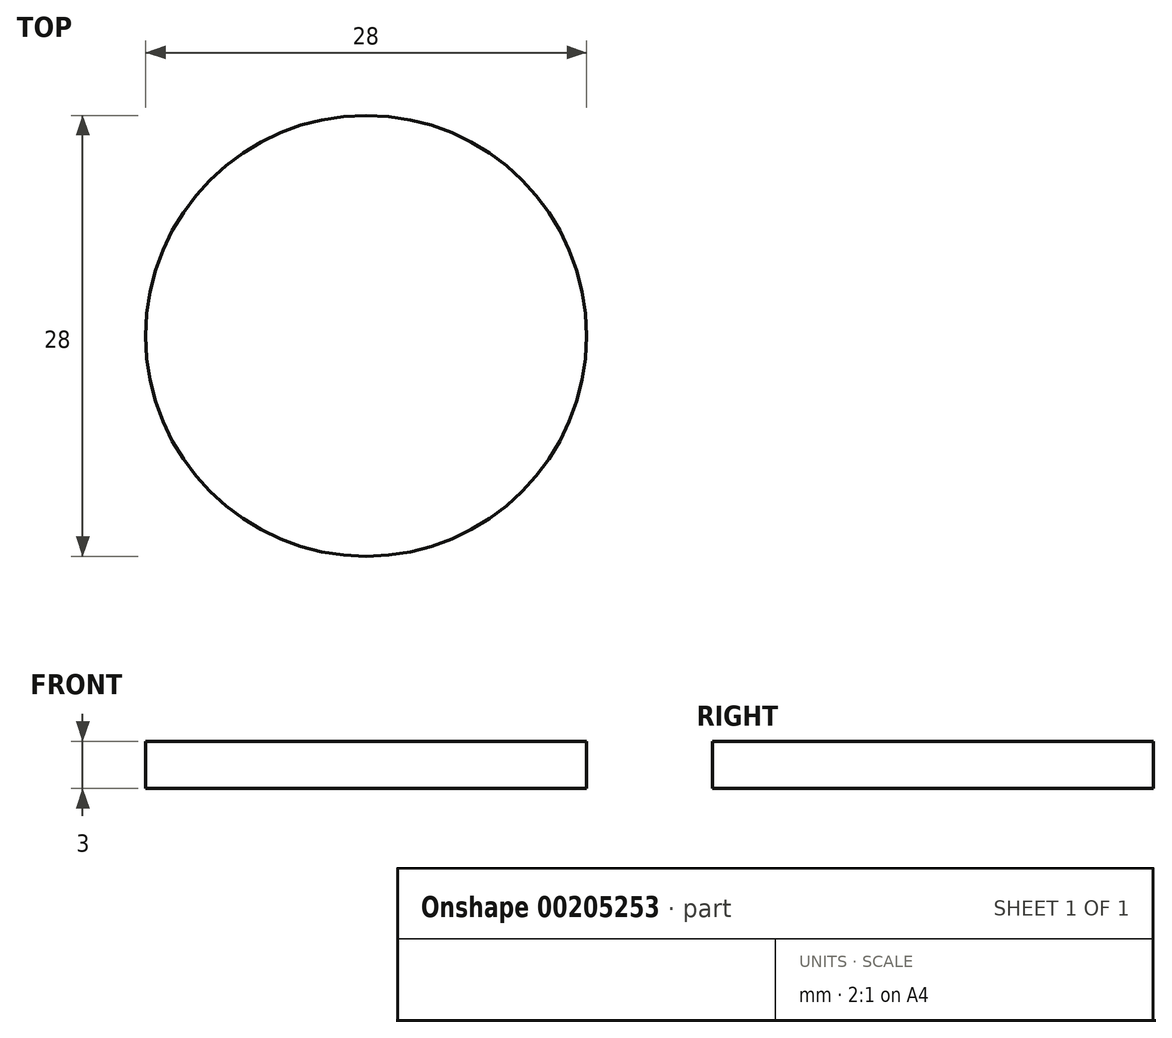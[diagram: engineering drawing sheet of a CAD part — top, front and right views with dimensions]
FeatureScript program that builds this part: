
annotation { "Feature Type Name" : "Feature", "Feature Type Description" : "" }
export const myFeature = defineFeature(function(context is Context, id is Id, definition is map)
    precondition{}
    {
        {
            var Q0;
            Q0=qCreatedBy(makeId("Top.planeOp"),FACE);
            var sketch = newSketch(context, id + "F0", { "sketchPlane" : qUnion([Q0])});
            skLineSegment(sketch, "E0", {"start": v(184.77, 212.37) * mm, "end": v(184.77, -227.26) * mm});
            skLineSegment(sketch, "E1", {"start": v(184.77, -227.26) * mm, "end": v(184.77, -233) * mm});
            skLineSegment(sketch, "E2", {"start": v(184.77, -233) * mm, "end": v(146.55, -233) * mm});
            skLineSegment(sketch, "E3", {"start": v(146.55, -233) * mm, "end": v(146.55, -227.26) * mm});
            skLineSegment(sketch, "E4", {"start": v(146.55, -227.26) * mm, "end": v(117.87, -227.26) * mm});
            skLineSegment(sketch, "E5", {"start": v(117.87, -227.26) * mm, "end": v(117.87, -233) * mm});
            skLineSegment(sketch, "E6", {"start": v(117.87, -233) * mm, "end": v(79.65, -233) * mm});
            skLineSegment(sketch, "E7", {"start": v(79.65, -233) * mm, "end": v(79.65, -227.26) * mm});
            skLineSegment(sketch, "E8", {"start": v(79.65, -227.26) * mm, "end": v(50.97, -227.26) * mm});
            skLineSegment(sketch, "E9", {"start": v(50.97, -227.26) * mm, "end": v(50.97, -233) * mm});
            skLineSegment(sketch, "E10", {"start": v(50.97, -233) * mm, "end": v(12.75, -233) * mm});
            skLineSegment(sketch, "E11", {"start": v(12.75, -233) * mm, "end": v(12.75, -227.26) * mm});
            skLineSegment(sketch, "E12", {"start": v(12.75, -227.26) * mm, "end": v(10.83, -225.35) * mm});
            skLineSegment(sketch, "E13", {"start": v(10.83, -225.35) * mm, "end": v(1.28, -215.79) * mm});
            skLineSegment(sketch, "E14", {"start": v(1.28, -215.79) * mm, "end": v(1.28, 200.9) * mm});
            skLineSegment(sketch, "E15", {"start": v(1.28, 200.9) * mm, "end": v(10.83, 210.46) * mm});
            skLineSegment(sketch, "E16", {"start": v(10.83, 210.46) * mm, "end": v(12.75, 212.37) * mm});
            skLineSegment(sketch, "E17", {"start": v(12.75, 212.37) * mm, "end": v(12.75, 212.37) * mm});
            skLineSegment(sketch, "E18", {"start": v(12.75, 212.37) * mm, "end": v(12.75, 218.1) * mm});
            skLineSegment(sketch, "E19", {"start": v(12.75, 218.1) * mm, "end": v(50.97, 218.1) * mm});
            skLineSegment(sketch, "E20", {"start": v(50.97, 218.1) * mm, "end": v(50.97, 212.37) * mm});
            skLineSegment(sketch, "E21", {"start": v(50.97, 212.37) * mm, "end": v(79.65, 212.37) * mm});
            skLineSegment(sketch, "E22", {"start": v(79.65, 212.37) * mm, "end": v(79.65, 218.1) * mm});
            skLineSegment(sketch, "E23", {"start": v(79.65, 218.1) * mm, "end": v(117.87, 218.1) * mm});
            skLineSegment(sketch, "E24", {"start": v(117.87, 218.1) * mm, "end": v(117.87, 212.37) * mm});
            skLineSegment(sketch, "E25", {"start": v(117.87, 212.37) * mm, "end": v(146.55, 212.37) * mm});
            skLineSegment(sketch, "E26", {"start": v(146.55, 212.37) * mm, "end": v(146.55, 218.1) * mm});
            skLineSegment(sketch, "E27", {"start": v(146.55, 218.1) * mm, "end": v(184.77, 218.1) * mm});
            skLineSegment(sketch, "E28", {"start": v(184.77, 218.1) * mm, "end": v(184.77, 212.37) * mm});
            skCircle(sketch, "E29", {"center": v(166.25, 204.4) * mm, "radius": 2.07 * mm});
            skCircle(sketch, "E30", {"center": v(115.56, 203.62) * mm, "radius": 4 * mm});
            skCircle(sketch, "E31", {"center": v(70.1, 203.62) * mm, "radius": 4 * mm});
            skCircle(sketch, "E32", {"center": v(115.56, 117.87) * mm, "radius": 4 * mm});
            skCircle(sketch, "E33", {"center": v(70.1, 117.87) * mm, "radius": 4 * mm});
            skLineSegment(sketch, "E34", {"start": v(70.1, 203.62) * mm, "end": v(115.56, 117.87) * mm, "construction": true});
            skLineSegment(sketch, "E35", {"start": v(115.56, 203.62) * mm, "end": v(70.1, 117.87) * mm, "construction": true});
            skCircle(sketch, "E36", {"center": v(92.83, 160.74) * mm, "radius": 14 * mm});
            skLineSegment(sketch, "E37", {"start": v(92.83, 160.74) * mm, "end": v(184.77, 160.74) * mm, "construction": true});
            skLineSegment(sketch, "E38", {"start": v(184.77, 160.74) * mm, "end": v(0.88, 160.74) * mm, "construction": true});
            skCircle(sketch, "E39", {"center": v(30.7, 204.4) * mm, "radius": 2.07 * mm});
            skCircle(sketch, "E40", {"center": v(30.54, -218.1) * mm, "radius": 2.07 * mm});
            skCircle(sketch, "E41", {"center": v(166.25, -218.1) * mm, "radius": 2.07 * mm});
            skLineSegment(sketch, "E42", {"start": v(1.28, 200.9) * mm, "end": v(1.28, -215.79) * mm});
            skLineSegment(sketch, "E43", {"start": v(1.28, -215.79) * mm, "end": v(12.75, -227.26) * mm});
            skLineSegment(sketch, "E44", {"start": v(12.75, -227.26) * mm, "end": v(12.75, -233) * mm});
            skLineSegment(sketch, "E45", {"start": v(12.75, -233) * mm, "end": v(50.97, -233) * mm});
            skSolve(sketch);
        }
        {
            var Q0;
            Q0=qCreatedBy(makeId("Top.planeOp"),FACE);
            var sketch = newSketch(context, id + "F1", { "sketchPlane" : qUnion([Q0])});
            skCircle(sketch, "E46", {"center": v(106.83, 93.87) * mm, "radius": 14 * mm});
            skCircle(sketch, "E47", {"center": v(68.33, 86.87) * mm, "radius": 14 * mm});
            skCircle(sketch, "E48", {"center": v(54.33, 53.87) * mm, "radius": 14 * mm});
            skCircle(sketch, "E49", {"center": v(92.83, 60.87) * mm, "radius": 14.61 * mm});
            skCircle(sketch, "E50", {"center": v(60.33, 18.37) * mm, "radius": 14 * mm});
            skCircle(sketch, "E51", {"center": v(98.83, 24.87) * mm, "radius": 14 * mm});
            skCircle(sketch, "E52", {"center": v(106.83, 93.87) * mm, "radius": 17.5 * mm, "construction": true});
            skCircle(sketch, "E53", {"center": v(107.03, -131.4) * mm, "radius": 14 * mm});
            skCircle(sketch, "E54", {"center": v(68.53, -138.4) * mm, "radius": 14 * mm});
            skCircle(sketch, "E55", {"center": v(54.53, -171.4) * mm, "radius": 14 * mm});
            skCircle(sketch, "E56", {"center": v(93.03, -164.4) * mm, "radius": 14.61 * mm});
            skCircle(sketch, "E57", {"center": v(60.53, -206.9) * mm, "radius": 14 * mm});
            skCircle(sketch, "E58", {"center": v(99.03, -200.4) * mm, "radius": 14 * mm});
            skCircle(sketch, "E59", {"center": v(107.03, -131.4) * mm, "radius": 17.5 * mm, "construction": true});
            skCircle(sketch, "E60", {"center": v(114.82, -21.64) * mm, "radius": 4.38 * mm, "construction": true});
            skCircle(sketch, "E61", {"center": v(69.35, -21.64) * mm, "radius": 4.38 * mm, "construction": true});
            skCircle(sketch, "E62", {"center": v(114.82, -107.4) * mm, "radius": 4.38 * mm, "construction": true});
            skCircle(sketch, "E63", {"center": v(69.35, -107.4) * mm, "radius": 4.38 * mm, "construction": true});
            skLineSegment(sketch, "E64", {"start": v(69.35, -21.64) * mm, "end": v(114.82, -107.4) * mm, "construction": true});
            skLineSegment(sketch, "E65", {"start": v(114.82, -21.64) * mm, "end": v(69.35, -107.4) * mm, "construction": true});
            skCircle(sketch, "E66", {"center": v(92.09, -64.52) * mm, "radius": 14.2 * mm, "construction": true});
            skCircle(sketch, "E67", {"center": v(60.53, -206.9) * mm, "radius": 17.5 * mm, "construction": true});
            skCircle(sketch, "E68", {"center": v(92.09, -64.52) * mm, "radius": 14 * mm});
            skCircle(sketch, "E69", {"center": v(69.35, -21.64) * mm, "radius": 4 * mm});
            skCircle(sketch, "E70", {"center": v(114.82, -21.64) * mm, "radius": 4 * mm});
            skCircle(sketch, "E71", {"center": v(69.35, -107.4) * mm, "radius": 4 * mm});
            skCircle(sketch, "E72", {"center": v(114.82, -107.4) * mm, "radius": 4 * mm});
            skSolve(sketch);
        }
        {
            var Q0;
            Q0=qCreatedBy(makeId("Top.planeOp"),FACE);
            var sketch = newSketch(context, id + "F2", { "sketchPlane" : qUnion([Q0])});
            skLineSegment(sketch, "E73.0", {"start": v(184.77, 212.37) * mm, "end": v(184.77, -227.26) * mm});
            skLineSegment(sketch, "E74.0", {"start": v(1.28, -215.79) * mm, "end": v(1.28, 200.9) * mm});
            skLineSegment(sketch, "E75", {"start": v(184.77, -7.44) * mm, "end": v(1.28, -7.44) * mm, "construction": true});
            skCircle(sketch, "E76", {"center": v(21.96, 41.37) * mm, "radius": 14 * mm});
            skCircle(sketch, "E77.MirrorC", {"center": v(21.96, -56.26) * mm, "radius": 14 * mm});
            skLineSegment(sketch, "E78.0", {"start": v(79.65, 212.37) * mm, "end": v(79.65, 218.1) * mm});
            skLineSegment(sketch, "E78.1", {"start": v(50.97, 212.37) * mm, "end": v(79.65, 212.37) * mm});
            skLineSegment(sketch, "E78.2", {"start": v(79.65, 218.1) * mm, "end": v(117.87, 218.1) * mm});
            skLineSegment(sketch, "E78.3", {"start": v(117.87, 218.1) * mm, "end": v(117.87, 212.37) * mm});
            skLineSegment(sketch, "E78.4", {"start": v(117.87, 212.37) * mm, "end": v(146.55, 212.37) * mm});
            skLineSegment(sketch, "E78.5", {"start": v(146.55, 212.37) * mm, "end": v(146.55, 218.1) * mm});
            skLineSegment(sketch, "E78.6", {"start": v(146.55, 218.1) * mm, "end": v(184.77, 218.1) * mm});
            skLineSegment(sketch, "E78.7", {"start": v(184.77, 218.1) * mm, "end": v(184.77, 212.37) * mm});
            skPoint(sketch, "E78.9", {"position": v(184.77, -233) * mm});
            skLineSegment(sketch, "E78.10", {"start": v(184.77, -227.26) * mm, "end": v(184.77, -233) * mm});
            skLineSegment(sketch, "E78.11", {"start": v(184.77, -233) * mm, "end": v(146.55, -233) * mm});
            skLineSegment(sketch, "E78.12", {"start": v(146.55, -233) * mm, "end": v(146.55, -227.26) * mm});
            skLineSegment(sketch, "E78.13", {"start": v(146.55, -227.26) * mm, "end": v(117.87, -227.26) * mm});
            skLineSegment(sketch, "E78.14", {"start": v(117.87, -227.26) * mm, "end": v(117.87, -233) * mm});
            skLineSegment(sketch, "E78.15", {"start": v(117.87, -233) * mm, "end": v(79.65, -233) * mm});
            skLineSegment(sketch, "E78.16", {"start": v(79.65, -233) * mm, "end": v(79.65, -227.26) * mm});
            skLineSegment(sketch, "E78.17", {"start": v(79.65, -227.26) * mm, "end": v(50.97, -227.26) * mm});
            skLineSegment(sketch, "E78.18", {"start": v(50.97, -227.26) * mm, "end": v(50.97, -233) * mm});
            skLineSegment(sketch, "E78.19", {"start": v(50.97, -233) * mm, "end": v(12.75, -233) * mm});
            skLineSegment(sketch, "E78.20", {"start": v(12.75, -233) * mm, "end": v(12.75, -227.26) * mm});
            skLineSegment(sketch, "E78.21", {"start": v(12.75, -227.26) * mm, "end": v(10.83, -225.35) * mm});
            skLineSegment(sketch, "E78.22", {"start": v(10.83, -225.35) * mm, "end": v(1.28, -215.79) * mm});
            skLineSegment(sketch, "E78.24", {"start": v(1.28, 200.9) * mm, "end": v(10.83, 210.46) * mm});
            skLineSegment(sketch, "E78.25", {"start": v(10.83, 210.46) * mm, "end": v(12.75, 212.37) * mm});
            skLineSegment(sketch, "E78.26", {"start": v(12.75, 212.37) * mm, "end": v(12.75, 218.1) * mm});
            skLineSegment(sketch, "E78.27", {"start": v(12.75, 218.1) * mm, "end": v(50.97, 218.1) * mm});
            skLineSegment(sketch, "E78.28", {"start": v(50.97, 218.1) * mm, "end": v(50.97, 212.37) * mm});
            skSolve(sketch);
        }
        {
            var Q0;
            Q0=qCreatedBy(makeId("Top.planeOp"),FACE);
            var sketch = newSketch(context, id + "F3", { "sketchPlane" : qUnion([Q0])});
            skLineSegment(sketch, "E79.0", {"start": v(1.28, -215.79) * mm, "end": v(1.28, 200.9) * mm});
            skLineSegment(sketch, "E80.0", {"start": v(146.55, -233) * mm, "end": v(146.55, -227.26) * mm});
            skLineSegment(sketch, "E80.1", {"start": v(184.77, -233) * mm, "end": v(146.55, -233) * mm});
            skLineSegment(sketch, "E80.2", {"start": v(184.77, -227.26) * mm, "end": v(184.77, -233) * mm});
            skLineSegment(sketch, "E80.3", {"start": v(184.77, 212.37) * mm, "end": v(184.77, -227.26) * mm});
            skLineSegment(sketch, "E80.4", {"start": v(184.77, 218.1) * mm, "end": v(184.77, 212.37) * mm});
            skLineSegment(sketch, "E80.5", {"start": v(146.55, 218.1) * mm, "end": v(184.77, 218.1) * mm});
            skLineSegment(sketch, "E80.6", {"start": v(146.55, 212.37) * mm, "end": v(146.55, 218.1) * mm});
            skLineSegment(sketch, "E80.7", {"start": v(117.87, 212.37) * mm, "end": v(146.55, 212.37) * mm});
            skLineSegment(sketch, "E80.8", {"start": v(117.87, 218.1) * mm, "end": v(117.87, 212.37) * mm});
            skLineSegment(sketch, "E80.9", {"start": v(79.65, 218.1) * mm, "end": v(117.87, 218.1) * mm});
            skLineSegment(sketch, "E80.10", {"start": v(79.65, 212.37) * mm, "end": v(79.65, 218.1) * mm});
            skLineSegment(sketch, "E80.11", {"start": v(50.97, 212.37) * mm, "end": v(79.65, 212.37) * mm});
            skLineSegment(sketch, "E80.12", {"start": v(50.97, 218.1) * mm, "end": v(50.97, 212.37) * mm});
            skLineSegment(sketch, "E80.13", {"start": v(12.75, 218.1) * mm, "end": v(50.97, 218.1) * mm});
            skLineSegment(sketch, "E80.14", {"start": v(12.75, 212.37) * mm, "end": v(12.75, 218.1) * mm});
            skLineSegment(sketch, "E80.15", {"start": v(10.83, 210.46) * mm, "end": v(12.75, 212.37) * mm});
            skLineSegment(sketch, "E80.16", {"start": v(1.28, 200.9) * mm, "end": v(10.83, 210.46) * mm});
            skLineSegment(sketch, "E80.18", {"start": v(10.83, -225.35) * mm, "end": v(1.28, -215.79) * mm});
            skPoint(sketch, "E80.19", {"position": v(10.83, -225.35) * mm});
            skLineSegment(sketch, "E80.20", {"start": v(12.75, -227.26) * mm, "end": v(10.83, -225.35) * mm});
            skLineSegment(sketch, "E80.21", {"start": v(12.75, -233) * mm, "end": v(12.75, -227.26) * mm});
            skLineSegment(sketch, "E80.22", {"start": v(50.97, -233) * mm, "end": v(12.75, -233) * mm});
            skLineSegment(sketch, "E80.23", {"start": v(50.97, -227.26) * mm, "end": v(50.97, -233) * mm});
            skLineSegment(sketch, "E80.24", {"start": v(79.65, -227.26) * mm, "end": v(50.97, -227.26) * mm});
            skLineSegment(sketch, "E80.25", {"start": v(79.65, -233) * mm, "end": v(79.65, -227.26) * mm});
            skLineSegment(sketch, "E80.26", {"start": v(117.87, -233) * mm, "end": v(79.65, -233) * mm});
            skLineSegment(sketch, "E80.27", {"start": v(117.87, -227.26) * mm, "end": v(117.87, -233) * mm});
            skLineSegment(sketch, "E80.28", {"start": v(146.55, -227.26) * mm, "end": v(117.87, -227.26) * mm});
            skPoint(sketch, "E80.29", {"position": v(11.79, -226.3) * mm});
            skLineSegment(sketch, "E81", {"start": v(184.77, -233) * mm, "end": v(184.77, 218.1) * mm});
            skLineSegment(sketch, "E82", {"start": v(184.77, 218.1) * mm, "end": v(146.55, 218.1) * mm});
            skLineSegment(sketch, "E83", {"start": v(117.87, 212.37) * mm, "end": v(117.87, 218.1) * mm});
            skLineSegment(sketch, "E84", {"start": v(79.65, 218.1) * mm, "end": v(79.65, 212.37) * mm});
            skLineSegment(sketch, "E85", {"start": v(79.65, 212.37) * mm, "end": v(50.97, 212.37) * mm});
            skLineSegment(sketch, "E86", {"start": v(50.97, 218.1) * mm, "end": v(12.75, 218.1) * mm});
            skLineSegment(sketch, "E87", {"start": v(12.75, 212.37) * mm, "end": v(1.28, 200.9) * mm});
            skLineSegment(sketch, "E88", {"start": v(1.28, 200.9) * mm, "end": v(1.28, -215.79) * mm});
            skLineSegment(sketch, "E89", {"start": v(1.28, -215.79) * mm, "end": v(12.75, -227.26) * mm});
            skLineSegment(sketch, "E90", {"start": v(12.75, -233) * mm, "end": v(50.97, -233) * mm});
            skLineSegment(sketch, "E91", {"start": v(50.97, -227.26) * mm, "end": v(79.65, -227.26) * mm});
            skLineSegment(sketch, "E92", {"start": v(79.65, -233) * mm, "end": v(117.87, -233) * mm});
            skLineSegment(sketch, "E93", {"start": v(117.87, -227.26) * mm, "end": v(146.55, -227.26) * mm});
            skLineSegment(sketch, "E94", {"start": v(146.55, -227.26) * mm, "end": v(146.55, -233) * mm});
            skLineSegment(sketch, "E95", {"start": v(146.55, -233) * mm, "end": v(184.77, -233) * mm});
            skSolve(sketch);
        }
        {
            var Q0;
            Q0=makeQuery(id+"F3.imprint","IMPRINT",FACE,{"disambiguationData":[TD([[makeQuery(id+"F3.imprint","IMPRINT",EDGE,{"derivedFrom":sQuery(id+"F3.wireOp",EDGE,"E80.18")}),-1.0]])]});
            extrude(context, id + "F4", {"entities" : qUnion([Q0]), "depth" : 3 * mm});
        }
        {
            var Q0;
            Q0=makeQuery(id+"F0.imprint","IMPRINT",FACE,{"disambiguationData":[TD([[makeQuery(id+"F0.imprint","IMPRINT",EDGE,{"derivedFrom":sQuery(id+"F0.wireOp",EDGE,"E39")}),1.0]])]});
            var Q1;
            Q1=makeQuery(id+"F0.imprint","IMPRINT",FACE,{"disambiguationData":[TD([[makeQuery(id+"F0.imprint","IMPRINT",EDGE,{"derivedFrom":sQuery(id+"F0.wireOp",EDGE,"E31")}),1.0]])]});
            var Q2;
            Q2=makeQuery(id+"F0.imprint","IMPRINT",FACE,{"disambiguationData":[TD([[makeQuery(id+"F0.imprint","IMPRINT",EDGE,{"derivedFrom":sQuery(id+"F0.wireOp",EDGE,"E30")}),1.0]])]});
            var Q3;
            Q3=makeQuery(id+"F0.imprint","IMPRINT",FACE,{"disambiguationData":[TD([[makeQuery(id+"F0.imprint","IMPRINT",EDGE,{"derivedFrom":sQuery(id+"F0.wireOp",EDGE,"E29")}),1.0]])]});
            var Q4;
            Q4=makeQuery(id+"F0.imprint","IMPRINT",FACE,{"disambiguationData":[TD([[makeQuery(id+"F0.imprint","IMPRINT",EDGE,{"derivedFrom":sQuery(id+"F0.wireOp",EDGE,"E36")}),1.0]])]});
            var Q5;
            Q5=makeQuery(id+"F0.imprint","IMPRINT",FACE,{"disambiguationData":[TD([[makeQuery(id+"F0.imprint","IMPRINT",EDGE,{"derivedFrom":sQuery(id+"F0.wireOp",EDGE,"E33")}),1.0]])]});
            var Q6;
            Q6=makeQuery(id+"F0.imprint","IMPRINT",FACE,{"disambiguationData":[TD([[makeQuery(id+"F0.imprint","IMPRINT",EDGE,{"derivedFrom":sQuery(id+"F0.wireOp",EDGE,"E32")}),1.0]])]});
            var Q7;
            Q7=makeQuery(id+"F1.imprint","IMPRINT",FACE,{"disambiguationData":[TD([[makeQuery(id+"F1.imprint","IMPRINT",EDGE,{"derivedFrom":sQuery(id+"F1.wireOp",EDGE,"E46")}),1.0]])]});
            var Q8;
            Q8=makeQuery(id+"F1.imprint","IMPRINT",FACE,{"disambiguationData":[TD([[makeQuery(id+"F1.imprint","IMPRINT",EDGE,{"derivedFrom":sQuery(id+"F1.wireOp",EDGE,"E47")}),1.0]])]});
            var Q9;
            Q9=makeQuery(id+"F1.imprint","IMPRINT",FACE,{"disambiguationData":[TD([[makeQuery(id+"F1.imprint","IMPRINT",EDGE,{"derivedFrom":sQuery(id+"F1.wireOp",EDGE,"E49")}),1.0]])]});
            var Q10;
            Q10=makeQuery(id+"F1.imprint","IMPRINT",FACE,{"disambiguationData":[TD([[makeQuery(id+"F1.imprint","IMPRINT",EDGE,{"derivedFrom":sQuery(id+"F1.wireOp",EDGE,"E51")}),1.0]])]});
            var Q11;
            Q11=makeQuery(id+"F1.imprint","IMPRINT",FACE,{"disambiguationData":[TD([[makeQuery(id+"F1.imprint","IMPRINT",EDGE,{"derivedFrom":sQuery(id+"F1.wireOp",EDGE,"E48")}),1.0]])]});
            var Q12;
            Q12=makeQuery(id+"F1.imprint","IMPRINT",FACE,{"disambiguationData":[TD([[makeQuery(id+"F1.imprint","IMPRINT",EDGE,{"derivedFrom":sQuery(id+"F1.wireOp",EDGE,"E50")}),1.0]])]});
            var Q13;
            Q13=makeQuery(id+"F2.imprint","IMPRINT",FACE,{"disambiguationData":[TD([[makeQuery(id+"F2.imprint","IMPRINT",EDGE,{"derivedFrom":sQuery(id+"F2.wireOp",EDGE,"E76")}),1.0]])]});
            var Q14;
            Q14=makeQuery(id+"F2.imprint","IMPRINT",FACE,{"disambiguationData":[TD([[makeQuery(id+"F2.imprint","IMPRINT",EDGE,{"derivedFrom":sQuery(id+"F2.wireOp",EDGE,"E77.MirrorC")}),-1.0]])]});
            var Q15;
            Q15=makeQuery(id+"F1.imprint","IMPRINT",FACE,{"disambiguationData":[TD([[makeQuery(id+"F1.imprint","IMPRINT",EDGE,{"derivedFrom":sQuery(id+"F1.wireOp",EDGE,"E53")}),1.0]])]});
            var Q16;
            Q16=makeQuery(id+"F1.imprint","IMPRINT",FACE,{"disambiguationData":[TD([[makeQuery(id+"F1.imprint","IMPRINT",EDGE,{"derivedFrom":sQuery(id+"F1.wireOp",EDGE,"E54")}),1.0]])]});
            var Q17;
            Q17=makeQuery(id+"F1.imprint","IMPRINT",FACE,{"disambiguationData":[TD([[makeQuery(id+"F1.imprint","IMPRINT",EDGE,{"derivedFrom":sQuery(id+"F1.wireOp",EDGE,"E55")}),1.0]])]});
            var Q18;
            Q18=makeQuery(id+"F1.imprint","IMPRINT",FACE,{"disambiguationData":[TD([[makeQuery(id+"F1.imprint","IMPRINT",EDGE,{"derivedFrom":sQuery(id+"F1.wireOp",EDGE,"E56")}),1.0]])]});
            var Q19;
            Q19=makeQuery(id+"F1.imprint","IMPRINT",FACE,{"disambiguationData":[TD([[makeQuery(id+"F1.imprint","IMPRINT",EDGE,{"derivedFrom":sQuery(id+"F1.wireOp",EDGE,"E58")}),1.0]])]});
            var Q20;
            Q20=makeQuery(id+"F1.imprint","IMPRINT",FACE,{"disambiguationData":[TD([[makeQuery(id+"F1.imprint","IMPRINT",EDGE,{"derivedFrom":sQuery(id+"F1.wireOp",EDGE,"E57")}),1.0]])]});
            var Q21;
            Q21=makeQuery(id+"F0.imprint","IMPRINT",FACE,{"disambiguationData":[TD([[makeQuery(id+"F0.imprint","IMPRINT",EDGE,{"derivedFrom":sQuery(id+"F0.wireOp",EDGE,"E40")}),1.0]])]});
            var Q22;
            Q22=makeQuery(id+"F0.imprint","IMPRINT",FACE,{"disambiguationData":[TD([[makeQuery(id+"F0.imprint","IMPRINT",EDGE,{"derivedFrom":sQuery(id+"F0.wireOp",EDGE,"E41")}),1.0]])]});
            var Q23;
            Q23=makeQuery(id+"F1.imprint","IMPRINT",FACE,{"disambiguationData":[TD([[makeQuery(id+"F1.imprint","IMPRINT",EDGE,{"derivedFrom":sQuery(id+"F1.wireOp",EDGE,"E68")}),1.0]])]});
            var Q24;
            Q24=makeQuery(id+"F1.imprint","IMPRINT",FACE,{"disambiguationData":[TD([[makeQuery(id+"F1.imprint","IMPRINT",EDGE,{"derivedFrom":sQuery(id+"F1.wireOp",EDGE,"E69")}),1.0]])]});
            var Q25;
            Q25=makeQuery(id+"F1.imprint","IMPRINT",FACE,{"disambiguationData":[TD([[makeQuery(id+"F1.imprint","IMPRINT",EDGE,{"derivedFrom":sQuery(id+"F1.wireOp",EDGE,"E70")}),1.0]])]});
            var Q26;
            Q26=makeQuery(id+"F1.imprint","IMPRINT",FACE,{"disambiguationData":[TD([[makeQuery(id+"F1.imprint","IMPRINT",EDGE,{"derivedFrom":sQuery(id+"F1.wireOp",EDGE,"E72")}),1.0]])]});
            var Q27;
            Q27=makeQuery(id+"F1.imprint","IMPRINT",FACE,{"disambiguationData":[TD([[makeQuery(id+"F1.imprint","IMPRINT",EDGE,{"derivedFrom":sQuery(id+"F1.wireOp",EDGE,"E71")}),1.0]])]});
            extrude(context, id + "F5", {"entities" : qUnion([Q0, Q1, Q2, Q3, Q4, Q5, Q6, Q7, Q8, Q9, Q10, Q11, Q12, Q13, Q14, Q15, Q16, Q17, Q18, Q19, Q20, Q21, Q22, Q23, Q24, Q25, Q26, Q27]), "operationType" : NewBodyOperationType.REMOVE, "depth" : 25 * mm});
        }
    });
